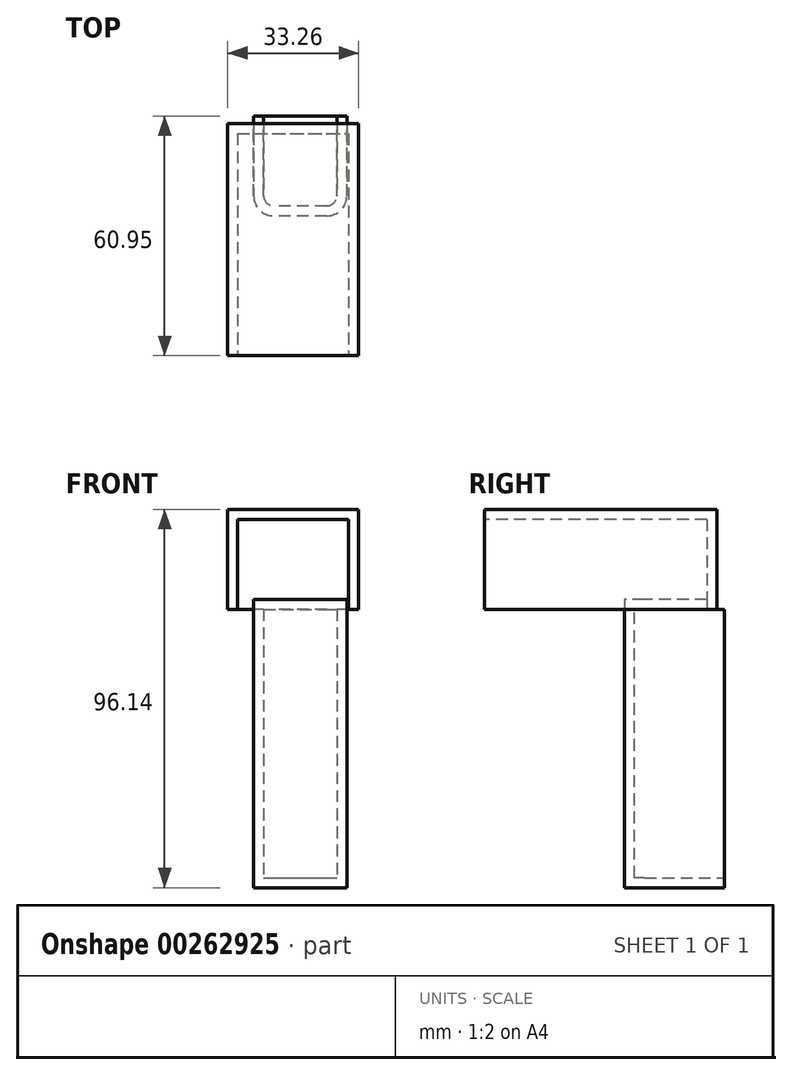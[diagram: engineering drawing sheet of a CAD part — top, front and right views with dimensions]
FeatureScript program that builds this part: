
annotation { "Feature Type Name" : "Feature", "Feature Type Description" : "" }
export const myFeature = defineFeature(function(context is Context, id is Id, definition is map)
    precondition{}
    {
        {
            var Q0;
            Q0=qCreatedBy(makeId("Front.planeOp"),FACE);
            var sketch = newSketch(context, id + "F0", { "sketchPlane" : qUnion([Q0])});
            skLineSegment(sketch, "E0.bottom", {"start": v(-23.65, 23.03) * mm, "end": v(0, 23.03) * mm});
            skLineSegment(sketch, "E0.top", {"start": v(-23.65, -70.74) * mm, "end": v(0, -70.74) * mm});
            skLineSegment(sketch, "E0.left", {"start": v(-23.65, 23.03) * mm, "end": v(-23.65, -70.74) * mm});
            skLineSegment(sketch, "E0.right", {"start": v(0, 23.03) * mm, "end": v(0, -70.74) * mm});
            skSolve(sketch);
        }
        {
            var Q0;
            Q0=makeQuery(id+"F0.imprint","IMPRINT",FACE,{"disambiguationData":[TD([[makeQuery(id+"F0.imprint","IMPRINT",EDGE,{"derivedFrom":sQuery(id+"F0.wireOp",EDGE,"E0.bottom")}),-1.0]])]});
            var Q1;
            Q1 = qSketchRegion(id + "F0", true);
            extrude(context, id + "F1", {"entities" : qUnion([Q0, Q1]), "depth" : 25.4 * mm});
        }
        {
            var Q0;
            Q0=makeQuery(id+"F1.opExtrude","CAP_EDGE",EDGE,{"disambiguationData":[OSD([sQuery(id+"F0.wireOp",EDGE,"E0.left")])],"isStart":false});
            fillet(context, id + "F2", {"entities" : qUnion([Q0]), "radius" : 5.08 * mm, "tangentPropagation" : true, "allowEdgeOverflow" : false});
        }
        {
            var Q0;
            Q0=makeQuery(id+"F1.opExtrude","CAP_EDGE",EDGE,{"disambiguationData":[OSD([sQuery(id+"F0.wireOp",EDGE,"E0.right")])],"isStart":false});
            fillet(context, id + "F3", {"entities" : qUnion([Q0]), "radius" : 5.08 * mm, "tangentPropagation" : true, "allowEdgeOverflow" : false});
        }
        {
            var Q0;
            Q0=makeQuery(id+"F1.opExtrude","CAP_FACE",FACE,{"disambiguationData":[OSD([sQuery(id+"F0.wireOp",EDGE,"E0.bottom"),sQuery(id+"F0.wireOp",EDGE,"E0.top"),sQuery(id+"F0.wireOp",EDGE,"E0.left"),sQuery(id+"F0.wireOp",EDGE,"E0.right")])],"isStart":true});
            shell(context, id + "F4", {"entities" : qUnion([Q0]), "thickness" : 2.54 * mm});
        }
        {
            var Q0;
            Q0=qCreatedBy(makeId("Top.planeOp"),FACE);
            var sketch = newSketch(context, id + "F5", { "sketchPlane" : qUnion([Q0])});
            skLineSegment(sketch, "E1.bottom", {"start": v(-30.26, 78.58) * mm, "end": v(3, 78.58) * mm});
            skLineSegment(sketch, "E1.top", {"start": v(-30.26, -121.97) * mm, "end": v(3, -121.97) * mm});
            skLineSegment(sketch, "E1.left", {"start": v(-30.26, 78.58) * mm, "end": v(-30.26, -121.97) * mm});
            skLineSegment(sketch, "E1.right", {"start": v(3, 78.58) * mm, "end": v(3, -121.97) * mm});
            skPoint(sketch, "E1.middle", {"position": v(-13.63, -21.7) * mm});
            skSolve(sketch);
        }
        {
            var Q0;
            Q0=makeQuery(id+"F5.imprint","IMPRINT",FACE,{"disambiguationData":[TD([[makeQuery(id+"F5.imprint","IMPRINT",EDGE,{"derivedFrom":sQuery(id+"F5.wireOp",EDGE,"E1.bottom")}),-1.0]])]});
            extrude(context, id + "F6", {"entities" : qUnion([Q0]), "operationType" : NewBodyOperationType.ADD, "depth" : 25.4 * mm});
        }
        {
            var Q0;
            Q0=makeQuery(id+"F6.opExtrude","SWEPT_FACE",FACE,{"disambiguationData":[OSD([sQuery(id+"F5.wireOp",EDGE,"E1.bottom")])]});
            extrude(context, id + "F7", {"entities" : qUnion([Q0]), "operationType" : NewBodyOperationType.REMOVE, "oppositeDirection" : true, "depth" : 80.49 * mm});
        }
        {
            var Q0;
            Q0=makeQuery(id+"F6.opExtrude","SWEPT_FACE",FACE,{"disambiguationData":[OSD([sQuery(id+"F5.wireOp",EDGE,"E1.top")])]});
            extrude(context, id + "F8", {"entities" : qUnion([Q0]), "operationType" : NewBodyOperationType.REMOVE, "oppositeDirection" : true, "depth" : 61.02 * mm});
        }
        {
            var Q0;
            Q0=makeQuery(id+"F8.boolean.opBoolean","COPY",FACE,{"derivedFrom":makeQuery(id+"F8.opExtrude","CAP_FACE",FACE,{"disambiguationData":[OSD([sQuery(id+"F5.wireOp",EDGE,"E1.top")])],"isStart":false})});
            var Q1;
            {var subQ0=sQuery(id+"F0.wireOp",EDGE,"E0.left");var subQ2=sQuery(id+"F5.wireOp",EDGE,"E1.top");var subQ3=sQuery(id+"F5.wireOp",EDGE,"E1.left");var subQ4=sQuery(id+"F5.wireOp",EDGE,"E1.bottom");var subQ5=sQuery(id+"F5.wireOp",EDGE,"E1.right");Q1=makeQuery(id+"F7.boolean.opBoolean","SPLIT",FACE,{"disambiguationData":[TD([makeQuery(id+"F1.opExtrude","SWEPT_FACE",FACE,{"disambiguationData":[OSD([subQ0])]})])],"derivedFrom":makeQuery(id+"F6.opExtrude","CAP_FACE",FACE,{"disambiguationData":[OSD([subQ4,subQ2,subQ3,subQ5])],"isStart":true})});}
            shell(context, id + "F9", {"entities" : qUnion([Q0, Q1]), "thickness" : 2.54 * mm});
        }
    });
